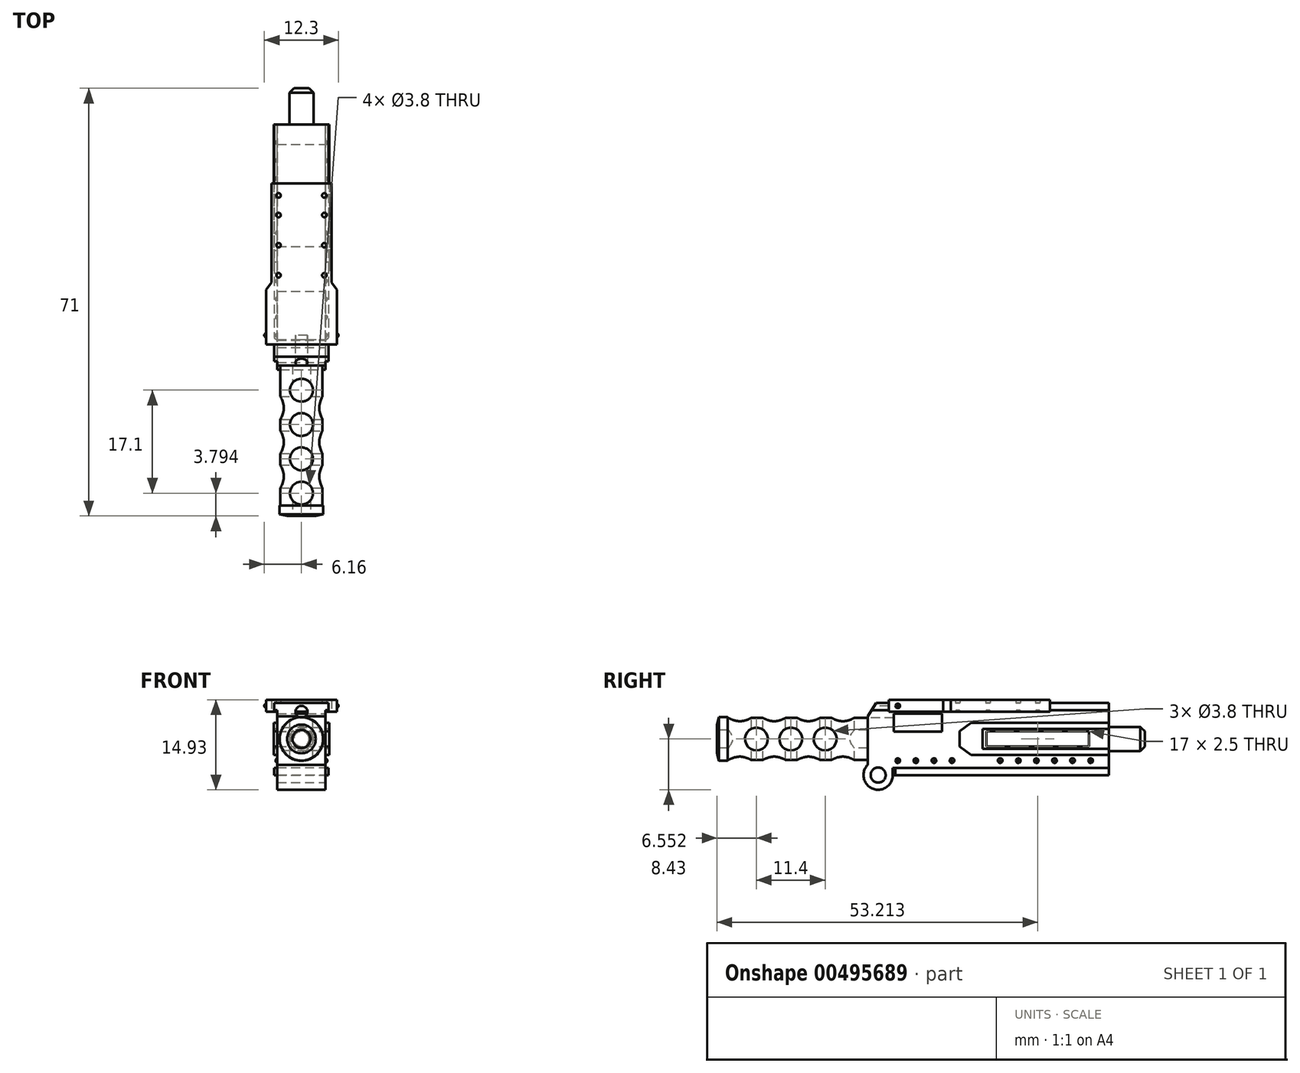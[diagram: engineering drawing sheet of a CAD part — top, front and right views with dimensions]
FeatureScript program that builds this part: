
annotation { "Feature Type Name" : "Feature", "Feature Type Description" : "" }
export const myFeature = defineFeature(function(context is Context, id is Id, definition is map)
    precondition{}
    {
        {
            var Q0;
            Q0=qCreatedBy(makeId("Front.planeOp"),FACE);
            var sketch = newSketch(context, id + "F0", { "sketchPlane" : qUnion([Q0])});
            skLineSegment(sketch, "E0.bottom", {"start": v(4, 6) * mm, "end": v(-4, 6) * mm});
            skLineSegment(sketch, "E0.top", {"start": v(4, -6) * mm, "end": v(-4, -6) * mm});
            skLineSegment(sketch, "E0.left", {"start": v(4, 6) * mm, "end": v(4, -6) * mm});
            skLineSegment(sketch, "E0.right", {"start": v(-4, 6) * mm, "end": v(-4, -6) * mm});
            skPoint(sketch, "E0.middle", {"position": v(0, 0) * mm});
            skSolve(sketch);
        }
        {
            var Q0;
            Q0=makeQuery(id+"F0.imprint","IMPRINT",FACE,{"disambiguationData":[TD([[makeQuery(id+"F0.imprint","IMPRINT",EDGE,{"derivedFrom":sQuery(id+"F0.wireOp",EDGE,"E0.bottom")}),1.0]])]});
            extrude(context, id + "F1", {"entities" : qUnion([Q0]), "depth" : 40 * mm});
        }
        {
            var Q0;
            Q0=makeQuery(id+"F1.opExtrude","CAP_FACE",FACE,{"disambiguationData":[OSD([sQuery(id+"F0.wireOp",EDGE,"E0.bottom"),sQuery(id+"F0.wireOp",EDGE,"E0.top"),sQuery(id+"F0.wireOp",EDGE,"E0.left"),sQuery(id+"F0.wireOp",EDGE,"E0.right")])],"isStart":false});
            var sketch = newSketch(context, id + "F2", { "sketchPlane" : qUnion([Q0])});
            skCircle(sketch, "E1", {"center": v(0, 0) * mm, "radius": 3.5 * mm});
            skSolve(sketch);
        }
        {
            var Q0;
            Q0 = qSketchRegion(id + "F2", true);
            extrude(context, id + "F3", {"entities" : qUnion([Q0]), "operationType" : NewBodyOperationType.ADD, "depth" : 25 * mm});
        }
        {
            var Q0;
            Q0=makeQuery(id+"F3.opExtrude","CAP_FACE",FACE,{"disambiguationData":[OSD([sQuery(id+"F2.wireOp",EDGE,"E1")])],"isStart":false});
            var sketch = newSketch(context, id + "F4", { "sketchPlane" : qUnion([Q0])});
            skCircle(sketch, "E2", {"center": v(0, 0) * mm, "radius": 1.5 * mm});
            skSolve(sketch);
        }
        {
            var Q0;
            Q0=makeQuery(id+"F4.imprint","IMPRINT",FACE,{"disambiguationData":[TD([[makeQuery(id+"F4.imprint","IMPRINT",EDGE,{"derivedFrom":sQuery(id+"F4.wireOp",EDGE,"E2")}),-1.0]])]});
            var sketch = newSketch(context, id + "F5", { "sketchPlane" : qUnion([Q0])});
            skCircle(sketch, "E3", {"center": v(0, 0) * mm, "radius": 3.62 * mm});
            skSolve(sketch);
        }
        {
            var Q0;
            Q0 = qSketchRegion(id + "F5", true);
            extrude(context, id + "F6", {"entities" : qUnion([Q0]), "operationType" : NewBodyOperationType.ADD, "oppositeDirection" : true, "depth" : 1.75 * mm, "offsetDistance" : 25 * mm});
        }
        {
            var Q0;
            Q0 = qSketchRegion(id + "F4", true);
            var Q1;
            Q1=makeQuery(id+"F1.opExtrude","CAP_FACE",FACE,{"disambiguationData":[OSD([sQuery(id+"F0.wireOp",EDGE,"E0.bottom"),sQuery(id+"F0.wireOp",EDGE,"E0.top"),sQuery(id+"F0.wireOp",EDGE,"E0.left"),sQuery(id+"F0.wireOp",EDGE,"E0.right")])],"isStart":false});
            extrude(context, id + "F7", {"entities" : qUnion([Q0]), "operationType" : NewBodyOperationType.REMOVE, "endBound" : BoundingType.UP_TO_SURFACE, "oppositeDirection" : true, "endBoundEntityFace" : qUnion([Q1]), "offsetDistance" : 25 * mm, "depth" : 35 * mm, "hasSecondDirection" : true, "secondDirectionOppositeDirection" : false, "secondDirectionDepth" : .5 * mm});
        }
        {
            var Q0;
            Q0=makeQuery(id+"F1.opExtrude","SWEPT_FACE",FACE,{"disambiguationData":[OSD([sQuery(id+"F0.wireOp",EDGE,"E0.left")])]});
            var sketch = newSketch(context, id + "F8", { "sketchPlane" : qUnion([Q0])});
            skCircle(sketch, "E4", {"center": v(-38.25, -6) * mm, "radius": 2.43 * mm});
            skSolve(sketch);
        }
        {
            var Q0;
            {var subQ0=sQuery(id+"F0.wireOp",EDGE,"E0.left");var subQ1=makeQuery(id+"F1.opExtrude","CAP_EDGE",EDGE,{"disambiguationData":[OSD([subQ0])],"isStart":false});var subQ4=sQuery(id+"F8.wireOp",EDGE,"E4");var subQ5=makeQuery(id+"F8.imprint","INTERSECT",VERTEX,{"derivedFrom":[subQ1,subQ4]});Q0=makeQuery(id+"F8.imprint","IMPRINT",FACE,{"disambiguationData":[TD([[makeQuery(id+"F8.imprint","IMPRINT",EDGE,{"disambiguationData":[TD([[subQ5,-1.0]])],"derivedFrom":subQ4}),1.0]])]});}
            extrude(context, id + "F9", {"entities" : qUnion([Q0]), "operationType" : NewBodyOperationType.ADD, "oppositeDirection" : true, "depth" : 8 * mm});
        }
        {
            var Q0;
            {var subQ0=sQuery(id+"F0.wireOp",EDGE,"E0.left");Q0=makeQuery(id+"F9.boolean.opBoolean","MERGE",FACE,{"derivedFrom":[makeQuery(id+"F1.opExtrude","SWEPT_FACE",FACE,{"disambiguationData":[OSD([subQ0])]}),makeQuery(id+"F9.opExtrude","CAP_FACE",FACE,{"disambiguationData":[OSD([sQuery(id+"F0.wireOp",EDGE,"E0.top"),subQ0,sQuery(id+"F8.wireOp",EDGE,"E4")])],"isStart":true})]});}
            var sketch = newSketch(context, id + "F10", { "sketchPlane" : qUnion([Q0])});
            skCircle(sketch, "E5", {"center": v(-38.25, -6) * mm, "radius": 1.25 * mm});
            skSolve(sketch);
        }
        {
            var Q0;
            Q0 = qSketchRegion(id + "F10", true);
            extrude(context, id + "F11", {"entities" : qUnion([Q0]), "operationType" : NewBodyOperationType.REMOVE, "endBound" : BoundingType.THROUGH_ALL, "oppositeDirection" : true, "depth" : 25 * mm});
        }
        {
            var Q0;
            {var subQ0=sQuery(id+"F0.wireOp",EDGE,"E0.left");Q0=makeQuery(id+"F9.boolean.opBoolean","MERGE",FACE,{"derivedFrom":[makeQuery(id+"F1.opExtrude","SWEPT_FACE",FACE,{"disambiguationData":[OSD([subQ0])]}),makeQuery(id+"F9.opExtrude","CAP_FACE",FACE,{"disambiguationData":[OSD([sQuery(id+"F0.wireOp",EDGE,"E0.top"),subQ0,sQuery(id+"F8.wireOp",EDGE,"E4")])],"isStart":true})]});}
            var sketch = newSketch(context, id + "F12", { "sketchPlane" : qUnion([Q0])});
            skLineSegment(sketch, "E6", {"start": v(-40, 6) * mm, "end": v(-35.67, 6) * mm});
            skLineSegment(sketch, "E7", {"start": v(-35.67, 6) * mm, "end": v(-35.67, 4.2) * mm});
            skLineSegment(sketch, "E8.bottom", {"start": v(-35.67, 4.2) * mm, "end": v(-27.67, 4.2) * mm});
            skLineSegment(sketch, "E8.top", {"start": v(-35.67, 1.2) * mm, "end": v(-27.67, 1.2) * mm});
            skLineSegment(sketch, "E8.left", {"start": v(-35.67, 4.2) * mm, "end": v(-35.67, 1.2) * mm});
            skLineSegment(sketch, "E8.right", {"start": v(-27.67, 4.2) * mm, "end": v(-27.67, 1.2) * mm});
            skLineSegment(sketch, "E9.bottom", {"start": v(-20.29, -1.25) * mm, "end": v(-3.29, -1.25) * mm});
            skLineSegment(sketch, "E9.top", {"start": v(-20.29, 1.25) * mm, "end": v(-3.29, 1.25) * mm});
            skLineSegment(sketch, "E9.left", {"start": v(-20.29, -1.25) * mm, "end": v(-20.29, 1.25) * mm});
            skLineSegment(sketch, "E9.right", {"start": v(-3.29, -1.25) * mm, "end": v(-3.29, 1.25) * mm});
            skPoint(sketch, "E9.middle", {"position": v(-11.79, 0) * mm});
            skSolve(sketch);
        }
        {
            var Q0;
            Q0=makeQuery(id+"F12.imprint","IMPRINT",FACE,{"disambiguationData":[TD([[makeQuery(id+"F12.imprint","IMPRINT",EDGE,{"derivedFrom":sQuery(id+"F12.wireOp",EDGE,"E9.bottom")}),1.0]])]});
            var Q1;
            Q1=makeQuery(id+"F12.imprint","IMPRINT",FACE,{"disambiguationData":[TD([[makeQuery(id+"F12.imprint","IMPRINT",EDGE,{"derivedFrom":sQuery(id+"F12.wireOp",EDGE,"E8.bottom")}),-1.0]])]});
            extrude(context, id + "F13", {"entities" : qUnion([Q0, Q1]), "operationType" : NewBodyOperationType.REMOVE, "endBound" : BoundingType.THROUGH_ALL, "oppositeDirection" : true, "depth" : 25 * mm});
        }
        {
            var Q0;
            Q0=makeQuery(id+"F1.opExtrude","SWEPT_FACE",FACE,{"disambiguationData":[OSD([sQuery(id+"F0.wireOp",EDGE,"E0.bottom")])]});
            var sketch = newSketch(context, id + "F14", { "sketchPlane" : qUnion([Q0])});
            skLineSegment(sketch, "E10", {"start": v(4, -29.35) * mm, "end": v(-4, -29.35) * mm, "construction": true});
            skLineSegment(sketch, "E11", {"start": v(4, -29.35) * mm, "end": v(4.5, -29.35) * mm});
            skLineSegment(sketch, "E12", {"start": v(-4, -29.35) * mm, "end": v(-4.5, -29.35) * mm});
            skLineSegment(sketch, "E13.bottom", {"start": v(4.5, -40) * mm, "end": v(-4.5, -40) * mm});
            skLineSegment(sketch, "E13.top", {"start": v(4.5, 0) * mm, "end": v(-4.5, 0) * mm});
            skLineSegment(sketch, "E13.left", {"start": v(4.5, -40) * mm, "end": v(4.5, 0) * mm});
            skLineSegment(sketch, "E13.right", {"start": v(-4.5, -40) * mm, "end": v(-4.5, 0) * mm});
            skSolve(sketch);
        }
        {
            var Q0;
            Q0 = qSketchRegion(id + "F14", true);
            extrude(context, id + "F15", {"entities" : qUnion([Q0]), "operationType" : NewBodyOperationType.ADD, "oppositeDirection" : true, "depth" : 1.2 * mm});
        }
        {
            var Q0;
            Q0=makeQuery(id+"F1.opExtrude","SWEPT_FACE",FACE,{"disambiguationData":[OSD([sQuery(id+"F0.wireOp",EDGE,"E0.top")])]});
            var sketch = newSketch(context, id + "F16", { "sketchPlane" : qUnion([Q0])});
            skLineSegment(sketch, "E14", {"start": v(4, 0) * mm, "end": v(4.5, 0) * mm});
            skLineSegment(sketch, "E15", {"start": v(-4, 35.82) * mm, "end": v(-4.5, 35.82) * mm});
            skLineSegment(sketch, "E16.bottom", {"start": v(4.5, 0) * mm, "end": v(-4.5, 0) * mm});
            skLineSegment(sketch, "E16.top", {"start": v(4.5, 35.82) * mm, "end": v(-4.5, 35.82) * mm});
            skLineSegment(sketch, "E16.left", {"start": v(4.5, 0) * mm, "end": v(4.5, 35.82) * mm});
            skLineSegment(sketch, "E16.right", {"start": v(-4.5, 0) * mm, "end": v(-4.5, 35.82) * mm});
            skLineSegment(sketch, "E17", {"start": v(4, 35.82) * mm, "end": v(4.5, 35.38) * mm});
            skLineSegment(sketch, "E18", {"start": v(-4.5, 35.38) * mm, "end": v(-4, 35.82) * mm});
            skSolve(sketch);
        }
        {
            var Q0;
            {var subQ4=sQuery(id+"F16.wireOp",EDGE,"E17");Q0=makeQuery(id+"F16.imprint","IMPRINT",FACE,{"disambiguationData":[TD([[makeQuery(id+"F16.imprint","IMPRINT",EDGE,{"derivedFrom":subQ4}),-1.0]])]});}
            var Q1;
            {var subQ1=sQuery(id+"F0.wireOp",EDGE,"E0.top");var subQ2=makeQuery(id+"F1.opExtrude","SWEPT_EDGE",EDGE,{"disambiguationData":[OSD([subQ1,sQuery(id+"F0.wireOp",EDGE,"E0.left")])]});Q1=makeQuery(id+"F16.imprint","IMPRINT",FACE,{"disambiguationData":[TD([[makeQuery(id+"F16.imprint","IMPRINT",EDGE,{"derivedFrom":subQ2}),-1.0]])]});}
            var Q2;
            {var subQ4=sQuery(id+"F16.wireOp",EDGE,"E18");Q2=makeQuery(id+"F16.imprint","IMPRINT",FACE,{"disambiguationData":[TD([[makeQuery(id+"F16.imprint","IMPRINT",EDGE,{"derivedFrom":subQ4}),-1.0]])]});}
            extrude(context, id + "F17", {"entities" : qUnion([Q0, Q1, Q2]), "operationType" : NewBodyOperationType.ADD, "oppositeDirection" : true, "depth" : 1.2 * mm});
        }
        {
            var Q0;
            Q0=makeQuery(id+"F15.boolean.opBoolean","MERGE",FACE,{"derivedFrom":[makeQuery(id+"F1.opExtrude","CAP_FACE",FACE,{"disambiguationData":[OSD([sQuery(id+"F0.wireOp",EDGE,"E0.bottom"),sQuery(id+"F0.wireOp",EDGE,"E0.top"),sQuery(id+"F0.wireOp",EDGE,"E0.left"),sQuery(id+"F0.wireOp",EDGE,"E0.right")])],"isStart":false}),makeQuery(id+"F15.opExtrude","SWEPT_FACE",FACE,{"disambiguationData":[OSD([sQuery(id+"F14.wireOp",EDGE,"E13.bottom")])]})]});
            var sketch = newSketch(context, id + "F18", { "sketchPlane" : qUnion([Q0])});
            skPoint(sketch, "E19.endSnap0", {"position": v(0, 6) * mm});
            skCircle(sketch, "E20", {"center": v(0, 4.5) * mm, "radius": 1 * mm});
            skSolve(sketch);
        }
        {
            var Q0;
            Q0=makeQuery(id+"F18.imprint","IMPRINT",FACE,{"disambiguationData":[TD([[makeQuery(id+"F18.imprint","IMPRINT",EDGE,{"derivedFrom":sQuery(id+"F18.wireOp",EDGE,"E20")}),1.0]])]});
            var Q1;
            Q1=sQuery(id+"F18.wireOp",EDGE,"E20");
            extrude(context, id + "F19", {"entities" : qUnion([Q0]), "operationType" : NewBodyOperationType.REMOVE, "surfaceEntities" : qUnion([Q1]), "oppositeDirection" : true, "offsetDistance" : 25 * mm, "depth" : 5 * mm});
        }
        {
            var Q0;
            Q0=makeQuery(id+"F10.imprint","IMPRINT",FACE,{"disambiguationData":[TD([[makeQuery(id+"F10.imprint","IMPRINT",EDGE,{"derivedFrom":sQuery(id+"F10.wireOp",EDGE,"E5")}),-1.0]])]});
            var sketch = newSketch(context, id + "F20", { "sketchPlane" : qUnion([Q0])});
            skLineSegment(sketch, "E21", {"start": v(0, 1.65) * mm, "end": v(-20.95, 1.65) * mm});
            skLineSegment(sketch, "E22", {"start": v(-20.95, 1.65) * mm, "end": v(-20.95, 0) * mm});
            skLineSegment(sketch, "E23.MirrorCS", {"start": v(0, -1.65) * mm, "end": v(-20.95, -1.65) * mm});
            skLineSegment(sketch, "E24.MirrorCS", {"start": v(-20.95, -1.65) * mm, "end": v(-20.95, 0) * mm});
            skLineSegment(sketch, "E25", {"start": v(0, 1.65) * mm, "end": v(0, 2.68) * mm});
            skLineSegment(sketch, "E26", {"start": v(0, 2.68) * mm, "end": v(-22.85, 2.68) * mm});
            skLineSegment(sketch, "E27", {"start": v(-22.85, 2.68) * mm, "end": v(-24.71, 1.26) * mm});
            skLineSegment(sketch, "E28", {"start": v(-24.71, 1.26) * mm, "end": v(-24.71, 0) * mm});
            skLineSegment(sketch, "E29.MirrorCS", {"start": v(0, -2.68) * mm, "end": v(-22.85, -2.68) * mm});
            skLineSegment(sketch, "E30.MirrorCS", {"start": v(-22.85, -2.68) * mm, "end": v(-24.71, -1.26) * mm});
            skLineSegment(sketch, "E31.MirrorCS", {"start": v(-24.71, -1.26) * mm, "end": v(-24.71, 0) * mm});
            skLineSegment(sketch, "E32", {"start": v(0, -2.68) * mm, "end": v(0, -1.65) * mm});
            skSolve(sketch);
        }
        {
            var Q0;
            Q0 = qSketchRegion(id + "F20", true);
            extrude(context, id + "F21", {"entities" : qUnion([Q0]), "operationType" : NewBodyOperationType.ADD, "depth" : .6 * mm, "hasSecondDirection" : true, "secondDirectionOppositeDirection" : true, "secondDirectionDepth" : 8.6 * mm});
        }
        {
            var Q0;
            Q0=makeQuery(id+"F21.boolean.opBoolean","MERGE",FACE,{"derivedFrom":[makeQuery(id+"F17.boolean.opBoolean","MERGE",FACE,{"derivedFrom":[makeQuery(id+"F15.boolean.opBoolean","MERGE",FACE,{"derivedFrom":[makeQuery(id+"F1.opExtrude","CAP_FACE",FACE,{"disambiguationData":[OSD([sQuery(id+"F0.wireOp",EDGE,"E0.bottom"),sQuery(id+"F0.wireOp",EDGE,"E0.top"),sQuery(id+"F0.wireOp",EDGE,"E0.left"),sQuery(id+"F0.wireOp",EDGE,"E0.right")])],"isStart":true}),makeQuery(id+"F15.opExtrude","SWEPT_FACE",FACE,{"disambiguationData":[OSD([sQuery(id+"F14.wireOp",EDGE,"E13.top")])]})]}),makeQuery(id+"F17.opExtrude","SWEPT_FACE",FACE,{"disambiguationData":[OSD([sQuery(id+"F16.wireOp",EDGE,"E16.bottom")])]})]}),makeQuery(id+"F21.opExtrude","SWEPT_FACE",FACE,{"disambiguationData":[OSD([sQuery(id+"F20.wireOp",EDGE,"E25")])]}),makeQuery(id+"F21.opExtrude","SWEPT_FACE",FACE,{"disambiguationData":[OSD([sQuery(id+"F20.wireOp",EDGE,"E32")])]})]});
            var sketch = newSketch(context, id + "F22", { "sketchPlane" : qUnion([Q0])});
            skCircle(sketch, "E33", {"center": v(0, 0) * mm, "radius": 2 * mm});
            skSolve(sketch);
        }
        {
            var Q0;
            Q0=qCreatedBy(makeId("Top.planeOp"),FACE);
            var sketch = newSketch(context, id + "F23", { "sketchPlane" : qUnion([Q0])});
            skLineSegment(sketch, "E34", {"start": v(0, -65) * mm, "end": v(0, -63.1) * mm});
            skLineSegment(sketch, "E35", {"start": v(0, -63.1) * mm, "end": v(0, -61.2) * mm});
            skLineSegment(sketch, "E36", {"start": v(0, -61.2) * mm, "end": v(0, -59.3) * mm});
            skLineSegment(sketch, "E37", {"start": v(0, -59.3) * mm, "end": v(0, -57.4) * mm});
            skLineSegment(sketch, "E38", {"start": v(0, -57.4) * mm, "end": v(0, -55.5) * mm});
            skLineSegment(sketch, "E39", {"start": v(0, -55.5) * mm, "end": v(0, -53.6) * mm});
            skLineSegment(sketch, "E40", {"start": v(0, -53.6) * mm, "end": v(0, -51.7) * mm});
            skLineSegment(sketch, "E41", {"start": v(0, -51.7) * mm, "end": v(0, -49.8) * mm});
            skLineSegment(sketch, "E42", {"start": v(0, -49.8) * mm, "end": v(0, -47.9) * mm});
            skLineSegment(sketch, "E43", {"start": v(0, -47.9) * mm, "end": v(0, -46) * mm});
            skLineSegment(sketch, "E44", {"start": v(0, -46) * mm, "end": v(0, -44.1) * mm});
            skLineSegment(sketch, "E45", {"start": v(0, -44.1) * mm, "end": v(0, -42.2) * mm});
            skCircle(sketch, "E46", {"center": v(0, -61.2) * mm, "radius": 1.9 * mm});
            skCircle(sketch, "E47", {"center": v(0, -55.5) * mm, "radius": 1.9 * mm});
            skCircle(sketch, "E48", {"center": v(0, -49.8) * mm, "radius": 1.9 * mm});
            skCircle(sketch, "E49", {"center": v(0, -44.1) * mm, "radius": 1.9 * mm});
            skSolve(sketch);
        }
        {
            var Q0;
            Q0 = qSketchRegion(id + "F23", true);
            extrude(context, id + "F24", {"entities" : qUnion([Q0]), "operationType" : NewBodyOperationType.REMOVE, "oppositeDirection" : true, "depth" : 6 * mm, "hasSecondDirection" : true, "secondDirectionOppositeDirection" : false, "secondDirectionDepth" : 6 * mm});
        }
        {
            var Q0;
            Q0=qCreatedBy(makeId("Right.planeOp"),FACE);
            var sketch = newSketch(context, id + "F25", { "sketchPlane" : qUnion([Q0])});
            skLineSegment(sketch, "E50", {"start": v(-81.72, 0) * mm, "end": v(-78.97, 0) * mm});
            skLineSegment(sketch, "E51", {"start": v(-65, 0) * mm, "end": v(-62.25, 0) * mm});
            skLineSegment(sketch, "E52", {"start": v(-62.25, 0) * mm, "end": v(-60.35, 0) * mm});
            skLineSegment(sketch, "E53", {"start": v(-60.35, 0) * mm, "end": v(-58.45, 0) * mm});
            skLineSegment(sketch, "E54", {"start": v(-58.45, 0) * mm, "end": v(-56.55, 0) * mm});
            skLineSegment(sketch, "E55", {"start": v(-56.55, 0) * mm, "end": v(-54.65, 0) * mm});
            skLineSegment(sketch, "E56", {"start": v(-54.65, 0) * mm, "end": v(-52.75, 0) * mm});
            skLineSegment(sketch, "E57", {"start": v(-52.75, 0) * mm, "end": v(-50.85, 0) * mm});
            skLineSegment(sketch, "E58", {"start": v(-50.85, 0) * mm, "end": v(-48.95, 0) * mm});
            skLineSegment(sketch, "E59", {"start": v(-48.95, 0) * mm, "end": v(-47.05, 0) * mm});
            skLineSegment(sketch, "E60", {"start": v(-47.05, 0) * mm, "end": v(-45.15, 0) * mm});
            skCircle(sketch, "E61", {"center": v(-58.45, 0) * mm, "radius": 1.9 * mm});
            skCircle(sketch, "E62", {"center": v(-52.75, 0) * mm, "radius": 1.9 * mm});
            skCircle(sketch, "E63", {"center": v(-47.05, 0) * mm, "radius": 1.9 * mm});
            skLineSegment(sketch, "E64", {"start": v(-47.05, 0) * mm, "end": v(-47.05, 4.24) * mm});
            skSolve(sketch);
        }
        {
            var Q0;
            Q0 = qSketchRegion(id + "F25", true);
            extrude(context, id + "F26", {"entities" : qUnion([Q0]), "operationType" : NewBodyOperationType.REMOVE, "endBound" : BoundingType.THROUGH_ALL, "oppositeDirection" : true, "depth" : 25 * mm, "hasSecondDirection" : true, "secondDirectionOppositeDirection" : false, "secondDirectionDepth" : 25 * mm});
        }
        {
            var Q0;
            Q0 = qSketchRegion(id + "F22", true);
            extrude(context, id + "F27", {"entities" : qUnion([Q0]), "operationType" : NewBodyOperationType.ADD, "offsetDistance" : 25 * mm, "depth" : 6 * mm});
        }
        {
            var Q0;
            Q0=makeQuery(id+"F10.imprint","IMPRINT",FACE,{"disambiguationData":[TD([[makeQuery(id+"F10.imprint","IMPRINT",EDGE,{"derivedFrom":sQuery(id+"F10.wireOp",EDGE,"E5")}),-1.0]])]});
            var sketch = newSketch(context, id + "F28", { "sketchPlane" : qUnion([Q0])});
            skLineSegment(sketch, "E65", {"start": v(-40.01, 3.72) * mm, "end": v(-38.55, 6.02) * mm});
            skLineSegment(sketch, "E66", {"start": v(-38.55, 6.02) * mm, "end": v(-40.05, 6.02) * mm});
            skLineSegment(sketch, "E67", {"start": v(-40.05, 6.02) * mm, "end": v(-40.01, 3.72) * mm});
            skSolve(sketch);
        }
        {
            var Q0;
            Q0 = qSketchRegion(id + "F28", true);
            extrude(context, id + "F29", {"entities" : qUnion([Q0]), "operationType" : NewBodyOperationType.REMOVE, "endBound" : BoundingType.THROUGH_ALL, "oppositeDirection" : true, "depth" : 25 * mm, "hasSecondDirection" : true, "secondDirectionBound" : SecondDirectionBoundingType.THROUGH_ALL, "secondDirectionOppositeDirection" : false, "secondDirectionDepth" : 25 * mm});
        }
        {
            var Q0;
            {var subQ1=sQuery(id+"F0.wireOp",EDGE,"E0.bottom");var subQ2=makeQuery(id+"F1.opExtrude","SWEPT_EDGE",EDGE,{"disambiguationData":[OSD([subQ1,sQuery(id+"F0.wireOp",EDGE,"E0.left")])]});var subQ7=sQuery(id+"F14.wireOp",EDGE,"E13.bottom");var subQ8=makeQuery(id+"F14.imprint","INTERSECT",VERTEX,{"derivedFrom":[subQ2,subQ7]});Q0=makeQuery(id+"F14.imprint","IMPRINT",FACE,{"disambiguationData":[TD([[makeQuery(id+"F14.imprint","IMPRINT",EDGE,{"disambiguationData":[TD([[subQ8,-1.0]])],"derivedFrom":subQ7}),-1.0]])]});}
            var sketch = newSketch(context, id + "F30", { "sketchPlane" : qUnion([Q0])});
            skLineSegment(sketch, "E68", {"start": v(0, -9.78) * mm, "end": v(-5, -9.78) * mm});
            skLineSegment(sketch, "E69", {"start": v(-5, -9.78) * mm, "end": v(-5, -26.2) * mm});
            skLineSegment(sketch, "E70", {"start": v(-5, -26.2) * mm, "end": v(-5.86, -27.45) * mm});
            skLineSegment(sketch, "E71", {"start": v(-5.86, -27.45) * mm, "end": v(-5.86, -36.5) * mm});
            skLineSegment(sketch, "E72", {"start": v(-5.86, -36.5) * mm, "end": v(0, -36.5) * mm});
            skLineSegment(sketch, "E73", {"start": v(0, 0) * mm, "end": v(0, -16.84) * mm, "construction": true});
            skLineSegment(sketch, "E74.MirrorCS", {"start": v(0, -9.78) * mm, "end": v(5, -9.78) * mm});
            skLineSegment(sketch, "E75.MirrorCS", {"start": v(5, -9.78) * mm, "end": v(5, -26.2) * mm});
            skLineSegment(sketch, "E76.MirrorCS", {"start": v(5.86, -36.5) * mm, "end": v(0, -36.5) * mm});
            skLineSegment(sketch, "E77.MirrorCS", {"start": v(5.86, -27.45) * mm, "end": v(5.86, -36.5) * mm});
            skLineSegment(sketch, "E78.MirrorCS", {"start": v(5, -26.2) * mm, "end": v(5.86, -27.45) * mm});
            skLineSegment(sketch, "E79", {"start": v(0, -9.78) * mm, "end": v(5, -9.78) * mm, "construction": true});
            skLineSegment(sketch, "E80", {"start": v(0, -9.78) * mm, "end": v(0, -11.78) * mm, "construction": true});
            skLineSegment(sketch, "E81", {"start": v(0, -11.78) * mm, "end": v(3.8, -11.78) * mm, "construction": true});
            skLineSegment(sketch, "E82", {"start": v(3.8, -11.78) * mm, "end": v(3.8, -15.04) * mm, "construction": true});
            skLineSegment(sketch, "E83", {"start": v(3.8, -15.04) * mm, "end": v(3.8, -17.54) * mm, "construction": true});
            skLineSegment(sketch, "E84", {"start": v(3.8, -17.54) * mm, "end": v(3.8, -20.04) * mm, "construction": true});
            skLineSegment(sketch, "E85", {"start": v(3.8, -20.04) * mm, "end": v(3.8, -22.54) * mm, "construction": true});
            skLineSegment(sketch, "E86", {"start": v(3.8, -22.54) * mm, "end": v(3.8, -25.04) * mm, "construction": true});
            skCircle(sketch, "E87", {"center": v(3.8, -11.78) * mm, "radius": 0.38 * mm});
            skCircle(sketch, "E88", {"center": v(3.8, -15.04) * mm, "radius": 0.38 * mm});
            skCircle(sketch, "E89", {"center": v(3.8, -20.04) * mm, "radius": 0.38 * mm});
            skCircle(sketch, "E90", {"center": v(3.8, -25.04) * mm, "radius": 0.38 * mm});
            skCircle(sketch, "E91.MirrorC", {"center": v(-3.8, -11.78) * mm, "radius": 0.38 * mm});
            skCircle(sketch, "E92.MirrorC", {"center": v(-3.8, -15.04) * mm, "radius": 0.38 * mm});
            skCircle(sketch, "E93.MirrorC", {"center": v(-3.8, -20.04) * mm, "radius": 0.38 * mm});
            skCircle(sketch, "E94.MirrorC", {"center": v(-3.8, -25.04) * mm, "radius": 0.38 * mm});
            skSolve(sketch);
        }
        {
            var Q0;
            Q0 = qSketchRegion(id + "F30", true);
            extrude(context, id + "F31", {"entities" : qUnion([Q0]), "operationType" : NewBodyOperationType.ADD, "depth" : 0.5 * mm, "offsetDistance" : 25 * mm, "hasSecondDirection" : true, "secondDirectionOppositeDirection" : true, "secondDirectionDepth" : 1.5 * mm});
        }
        {
            var Q0;
            Q0=makeQuery(id+"F31.opExtrude","SWEPT_FACE",FACE,{"disambiguationData":[OSD([sQuery(id+"F30.wireOp",EDGE,"E71")])]});
            var sketch = newSketch(context, id + "F32", { "sketchPlane" : qUnion([Q0])});
            skLineSegment(sketch, "E95", {"start": v(36.5, 4.5) * mm, "end": v(36.5, 5.5) * mm, "construction": true});
            skLineSegment(sketch, "E96", {"start": v(36.5, 5.5) * mm, "end": v(35, 5.5) * mm, "construction": true});
            skCircle(sketch, "E97", {"center": v(35, 5.5) * mm, "radius": 0.38 * mm});
            skSolve(sketch);
        }
        {
            var Q0;
            Q0=makeQuery(id+"F32.imprint","IMPRINT",FACE,{"disambiguationData":[TD([[makeQuery(id+"F32.imprint","IMPRINT",EDGE,{"derivedFrom":sQuery(id+"F32.wireOp",EDGE,"E97")}),1.0]])]});
            extrude(context, id + "F33", {"entities" : qUnion([Q0]), "operationType" : NewBodyOperationType.ADD, "depth" : 0.3 * mm, "offsetDistance" : 25 * mm, "hasSecondDirection" : true, "secondDirectionOppositeDirection" : true, "secondDirectionDepth" : 12 * mm});
        }
        {
            var Q0;
            Q0=makeQuery(id+"F33.opExtrude","CAP_EDGE",EDGE,{"disambiguationData":[OSD([sQuery(id+"F32.wireOp",EDGE,"E97")])],"isStart":false});
            var Q1;
            Q1=makeQuery(id+"F33.opExtrude","CAP_EDGE",EDGE,{"disambiguationData":[OSD([sQuery(id+"F32.wireOp",EDGE,"E97")])],"isStart":true});
            fillet(context, id + "F34", {"entities" : qUnion([Q0, Q1]), "tangentPropagation" : true, "crossSection" : FilletCrossSection.CONIC, "radius" : 0.3 * mm, "rho" : 0.25, "defaultsChanged" : false, "vertexSettings" : [], "allowEdgeOverflow" : false});
        }
        {
            var Q0;
            Q0=makeQuery(id+"F27.opExtrude","CAP_EDGE",EDGE,{"disambiguationData":[OSD([sQuery(id+"F22.wireOp",EDGE,"E33")])],"isStart":false});
            chamfer(context, id + "F35", {"entities" : qUnion([Q0]), "width" : 0.75 * mm, "tangentPropagation" : true});
        }
        {
            var Q0;
            Q0=makeQuery(id+"F10.imprint","IMPRINT",FACE,{"disambiguationData":[TD([[makeQuery(id+"F10.imprint","IMPRINT",EDGE,{"derivedFrom":sQuery(id+"F10.wireOp",EDGE,"E5")}),-1.0]])]});
            var sketch = newSketch(context, id + "F36", { "sketchPlane" : qUnion([Q0])});
            skLineSegment(sketch, "E98", {"start": v(0, 0) * mm, "end": v(0, -3.6) * mm, "construction": true});
            skLineSegment(sketch, "E99", {"start": v(0, -3.6) * mm, "end": v(-3, -3.6) * mm, "construction": true});
            skLineSegment(sketch, "E100", {"start": v(-3, -3.6) * mm, "end": v(-6, -3.6) * mm, "construction": true});
            skLineSegment(sketch, "E101", {"start": v(-6, -3.6) * mm, "end": v(-9, -3.6) * mm, "construction": true});
            skLineSegment(sketch, "E102", {"start": v(-9, -3.6) * mm, "end": v(-12, -3.6) * mm, "construction": true});
            skLineSegment(sketch, "E103", {"start": v(-12, -3.6) * mm, "end": v(-15, -3.6) * mm, "construction": true});
            skLineSegment(sketch, "E104", {"start": v(-15, -3.6) * mm, "end": v(-18, -3.6) * mm, "construction": true});
            skLineSegment(sketch, "E105", {"start": v(-18, -3.6) * mm, "end": v(-26, -3.6) * mm, "construction": true});
            skPoint(sketch, "E105.endSnap0", {"position": v(-16.5, -3.6) * mm});
            skLineSegment(sketch, "E106", {"start": v(-26, -3.6) * mm, "end": v(-29, -3.6) * mm, "construction": true});
            skLineSegment(sketch, "E107", {"start": v(-29, -3.6) * mm, "end": v(-32, -3.6) * mm, "construction": true});
            skLineSegment(sketch, "E108", {"start": v(-32, -3.6) * mm, "end": v(-35, -3.6) * mm, "construction": true});
            skCircle(sketch, "E109", {"center": v(-3, -3.6) * mm, "radius": 0.38 * mm});
            skCircle(sketch, "E110", {"center": v(-6, -3.6) * mm, "radius": 0.38 * mm});
            skCircle(sketch, "E111", {"center": v(-9, -3.6) * mm, "radius": 0.38 * mm});
            skCircle(sketch, "E112", {"center": v(-12, -3.6) * mm, "radius": 0.38 * mm});
            skCircle(sketch, "E113", {"center": v(-15, -3.6) * mm, "radius": 0.38 * mm});
            skCircle(sketch, "E114", {"center": v(-18, -3.6) * mm, "radius": 0.38 * mm});
            skCircle(sketch, "E115", {"center": v(-26, -3.6) * mm, "radius": 0.38 * mm});
            skCircle(sketch, "E116", {"center": v(-29, -3.6) * mm, "radius": 0.38 * mm});
            skCircle(sketch, "E117", {"center": v(-32, -3.6) * mm, "radius": 0.37 * mm});
            skCircle(sketch, "E118", {"center": v(-35, -3.6) * mm, "radius": 0.38 * mm});
            skSolve(sketch);
        }
        {
            var Q0;
            Q0 = qSketchRegion(id + "F36", true);
            extrude(context, id + "F37", {"entities" : qUnion([Q0]), "operationType" : NewBodyOperationType.ADD, "depth" : 0.3 * mm, "offsetDistance" : 25 * mm, "hasSecondDirection" : true, "secondDirectionOppositeDirection" : true, "secondDirectionDepth" : 8.3 * mm});
        }
        {
            var Q0;
            Q0=makeQuery(id+"F37.opExtrude","CAP_EDGE",EDGE,{"disambiguationData":[OSD([sQuery(id+"F36.wireOp",EDGE,"E118")])],"isStart":false});
            var Q1;
            Q1=makeQuery(id+"F37.opExtrude","CAP_EDGE",EDGE,{"disambiguationData":[OSD([sQuery(id+"F36.wireOp",EDGE,"E117")])],"isStart":false});
            var Q2;
            Q2=makeQuery(id+"F37.opExtrude","CAP_EDGE",EDGE,{"disambiguationData":[OSD([sQuery(id+"F36.wireOp",EDGE,"E116")])],"isStart":false});
            var Q3;
            Q3=makeQuery(id+"F37.opExtrude","CAP_EDGE",EDGE,{"disambiguationData":[OSD([sQuery(id+"F36.wireOp",EDGE,"E115")])],"isStart":false});
            var Q4;
            Q4=makeQuery(id+"F37.opExtrude","CAP_EDGE",EDGE,{"disambiguationData":[OSD([sQuery(id+"F36.wireOp",EDGE,"E114")])],"isStart":false});
            var Q5;
            Q5=makeQuery(id+"F37.opExtrude","CAP_EDGE",EDGE,{"disambiguationData":[OSD([sQuery(id+"F36.wireOp",EDGE,"E113")])],"isStart":false});
            var Q6;
            Q6=makeQuery(id+"F37.opExtrude","CAP_EDGE",EDGE,{"disambiguationData":[OSD([sQuery(id+"F36.wireOp",EDGE,"E112")])],"isStart":false});
            var Q7;
            Q7=makeQuery(id+"F37.opExtrude","CAP_EDGE",EDGE,{"disambiguationData":[OSD([sQuery(id+"F36.wireOp",EDGE,"E111")])],"isStart":false});
            var Q8;
            Q8=makeQuery(id+"F37.opExtrude","CAP_EDGE",EDGE,{"disambiguationData":[OSD([sQuery(id+"F36.wireOp",EDGE,"E110")])],"isStart":false});
            var Q9;
            Q9=makeQuery(id+"F37.opExtrude","CAP_EDGE",EDGE,{"disambiguationData":[OSD([sQuery(id+"F36.wireOp",EDGE,"E109")])],"isStart":false});
            var Q10;
            Q10=makeQuery(id+"F37.opExtrude","CAP_EDGE",EDGE,{"disambiguationData":[OSD([sQuery(id+"F36.wireOp",EDGE,"E109")])],"isStart":true});
            var Q11;
            Q11=makeQuery(id+"F37.opExtrude","CAP_EDGE",EDGE,{"disambiguationData":[OSD([sQuery(id+"F36.wireOp",EDGE,"E110")])],"isStart":true});
            var Q12;
            Q12=makeQuery(id+"F37.opExtrude","CAP_EDGE",EDGE,{"disambiguationData":[OSD([sQuery(id+"F36.wireOp",EDGE,"E111")])],"isStart":true});
            var Q13;
            Q13=makeQuery(id+"F37.opExtrude","CAP_EDGE",EDGE,{"disambiguationData":[OSD([sQuery(id+"F36.wireOp",EDGE,"E112")])],"isStart":true});
            var Q14;
            Q14=makeQuery(id+"F37.opExtrude","CAP_EDGE",EDGE,{"disambiguationData":[OSD([sQuery(id+"F36.wireOp",EDGE,"E113")])],"isStart":true});
            var Q15;
            Q15=makeQuery(id+"F37.opExtrude","CAP_EDGE",EDGE,{"disambiguationData":[OSD([sQuery(id+"F36.wireOp",EDGE,"E114")])],"isStart":true});
            var Q16;
            Q16=makeQuery(id+"F37.opExtrude","CAP_EDGE",EDGE,{"disambiguationData":[OSD([sQuery(id+"F36.wireOp",EDGE,"E115")])],"isStart":true});
            var Q17;
            Q17=makeQuery(id+"F37.opExtrude","CAP_EDGE",EDGE,{"disambiguationData":[OSD([sQuery(id+"F36.wireOp",EDGE,"E116")])],"isStart":true});
            var Q18;
            Q18=makeQuery(id+"F37.opExtrude","CAP_EDGE",EDGE,{"disambiguationData":[OSD([sQuery(id+"F36.wireOp",EDGE,"E117")])],"isStart":true});
            var Q19;
            Q19=makeQuery(id+"F37.opExtrude","CAP_EDGE",EDGE,{"disambiguationData":[OSD([sQuery(id+"F36.wireOp",EDGE,"E118")])],"isStart":true});
            fillet(context, id + "F38", {"entities" : qUnion([Q0, Q1, Q2, Q3, Q4, Q5, Q6, Q7, Q8, Q9, Q10, Q11, Q12, Q13, Q14, Q15, Q16, Q17, Q18, Q19]), "tangentPropagation" : true, "crossSection" : FilletCrossSection.CONIC, "radius" : 0.3 * mm, "rho" : .25, "defaultsChanged" : false, "vertexSettings" : [], "allowEdgeOverflow" : false});
        }
        {
            var Q0;
            Q0=makeQuery(id+"F6.opExtrude","CAP_EDGE",EDGE,{"disambiguationData":[OSD([sQuery(id+"F5.wireOp",EDGE,"E3")])],"isStart":true});
            chamfer(context, id + "F39", {"entities" : qUnion([Q0]), "chamferType" : ChamferType.TWO_OFFSETS, "width1" : 1.25 * mm, "oppositeDirection" : false, "width2" : .3 * mm, "tangentPropagation" : true});
        }
    });
